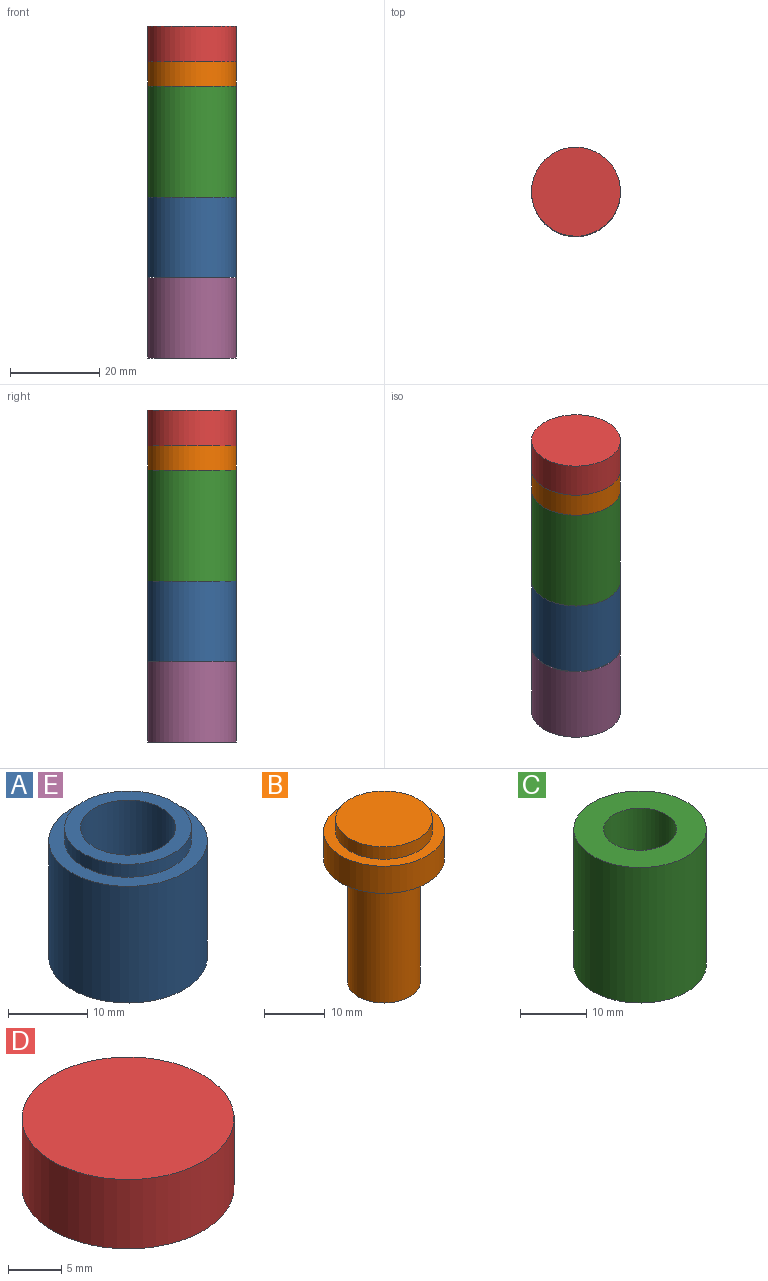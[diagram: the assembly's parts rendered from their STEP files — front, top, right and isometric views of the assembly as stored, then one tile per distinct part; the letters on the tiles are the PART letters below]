
ASSEMBLY  parts=5 mates=4
PART A: 8 faces, bbox 20x20x20 mm
  f0: cylinder r=10mm len=20mm, axis (0,0,1), area 1131mm2, adj f3,f5
  f1: plane 16x16mm, normal (0,0,1), area 88mm2, adj f2,f4
  f2: cylinder r=6mm len=17.5mm, axis (0,0,1), area 659.7mm2, adj f1,f7
  f3: plane 20x20mm, normal (0,0,-1), area 113.1mm2, adj f0,f6
  f4: cylinder r=8mm len=16mm, axis (0,0,1), area 100.5mm2, adj f1,f5
  f5: plane 20x20mm, normal (0,0,1), area 113.1mm2, adj f0,f4
  f6: cylinder r=8mm len=16mm, axis (0,0,1), area 125.7mm2, adj f3,f7
  f7: plane 16x16mm, normal (0,0,-1), area 88mm2, adj f2,f6
PART B: 7 faces, bbox 20x20x33 mm
  f0: cylinder r=10mm len=20mm, axis (0,0,-1), area 345.6mm2, adj f2,f5
  f1: cylinder r=6mm len=25mm, axis (0,0,-1), area 942.5mm2, adj f2,f3
  f2: plane 20x20mm, normal (0,0,-1), area 201.1mm2, adj f0,f1
  f3: plane 12x12mm, normal (0,0,-1), area 113.1mm2, adj f1
  f4: cylinder r=8mm len=16mm, axis (0,0,-1), area 125.7mm2, adj f5,f6
  f5: plane 20x20mm, normal (0,0,1), area 113.1mm2, adj f0,f4
  f6: plane 16x16mm, normal (0,0,1), area 201.1mm2, adj f4
PART C: 8 faces, bbox 20x20x25 mm
  f0: cylinder r=10mm len=25mm, axis (0,0,-1), area 1570.8mm2, adj f1,f2
  f1: plane 20x20mm, normal (0,0,1), area 219.1mm2, adj f0,f5
  f2: plane 20x20mm, normal (0,0,-1), area 113.1mm2, adj f0,f6
  f3: cylinder r=6mm len=12.5mm, axis (0,0,-1), area 471.2mm2, adj f4,f7
  f4: plane 12x12mm, normal (0,0,-1), area 18.1mm2, adj f3,f5
  f5: cylinder r=5.5mm len=11mm, axis (0,0,-1), area 345.6mm2, adj f1,f4
  f6: cylinder r=8mm len=16mm, axis (0,0,-1), area 125.7mm2, adj f2,f7
  f7: plane 16x16mm, normal (0,0,-1), area 88mm2, adj f3,f6
PART D: 5 faces, bbox 20x20x8 mm
  f0: cylinder r=10mm len=20mm, axis (0,0,-1), area 502.7mm2, adj f1,f2
  f1: plane 20x20mm, normal (0,0,1), area 314.2mm2, adj f0
  f2: plane 20x20mm, normal (0,0,-1), area 113.1mm2, adj f0,f3
  f3: cylinder r=8mm len=16mm, axis (0,0,-1), area 125.7mm2, adj f2,f4
  f4: plane 16x16mm, normal (0,0,-1), area 201.1mm2, adj f3
PART E: same geometry as A
PLACE A t=(32.54,31.05,-7.33)mm
PLACE B t=(32.54,31.05,-54.33)mm
PLACE C t=(32.54,31.05,-19.33)mm
PLACE D t=(32.54,31.05,-60.83)mm
PLACE E t=(32.54,31.05,-25.43)mm fixed
MATE slider E.f2 <-> A.f2  axis (0,0,1) through (32.54,31.05,-35.43)mm
MATE slider C.f5 <-> B.f1  axis (0,0,-1) through (32.54,31.05,5.67)mm
MATE slider B.f4 <-> D.f0  axis (0,0,1) through (32.54,31.05,11.17)mm
MATE slider A.f2 <-> C.f3  axis (0,0,1) through (32.54,31.05,-17.33)mm
